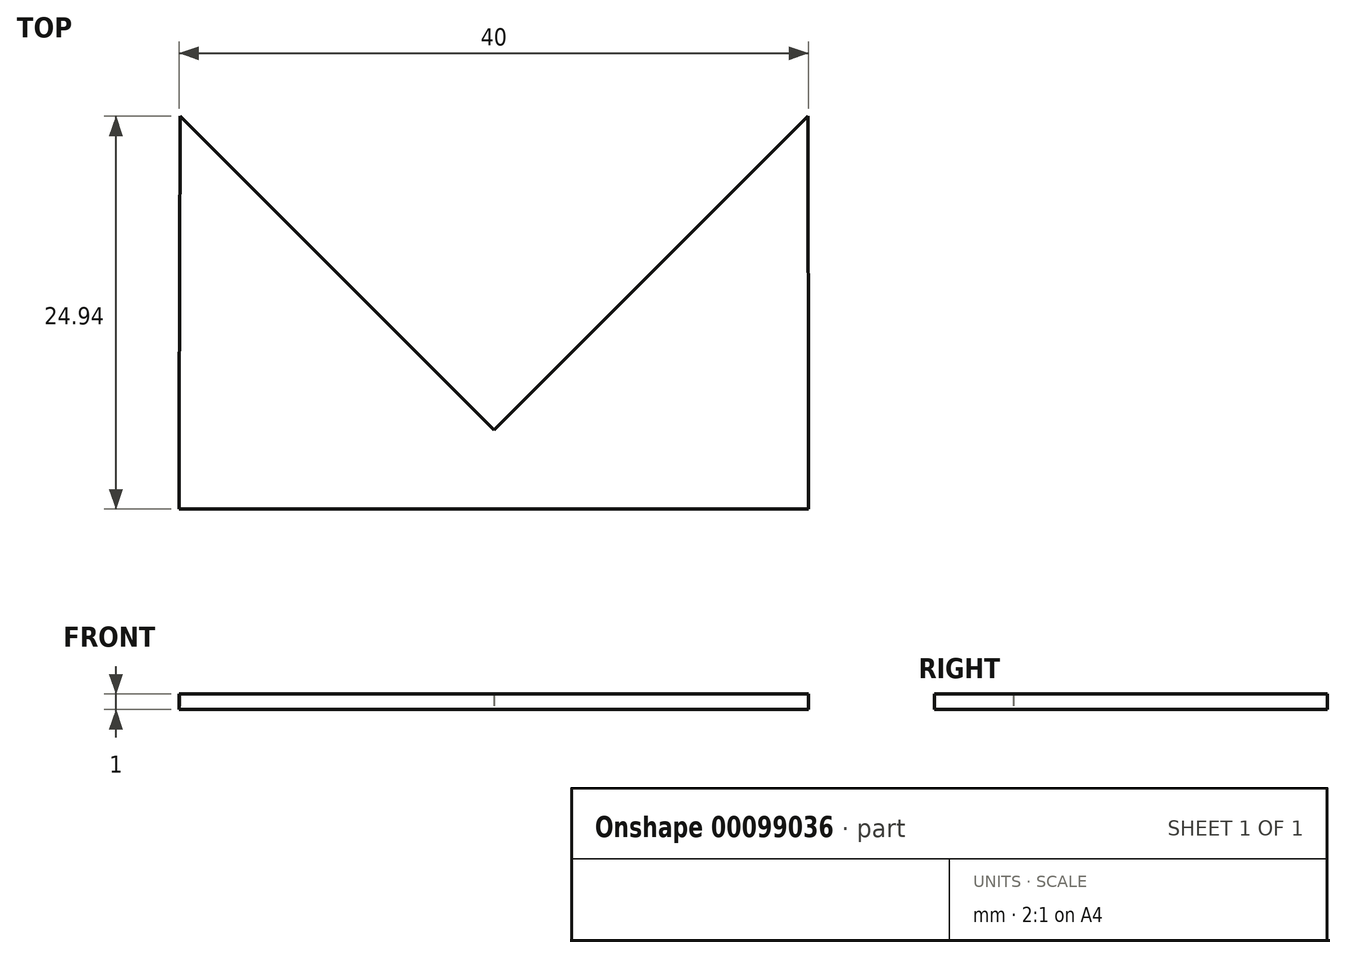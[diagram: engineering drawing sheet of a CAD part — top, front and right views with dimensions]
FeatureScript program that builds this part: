
annotation { "Feature Type Name" : "Feature", "Feature Type Description" : "" }
export const myFeature = defineFeature(function(context is Context, id is Id, definition is map)
    precondition{}
    {
        {
            var Q0;
            Q0=qCreatedBy(makeId("Top.planeOp"),FACE);
            var sketch = newSketch(context, id + "F0", { "sketchPlane" : qUnion([Q0])});
            skLineSegment(sketch, "E0.bottom", {"start": v(0, 0) * mm, "end": v(-20, 0) * mm});
            skLineSegment(sketch, "E0.top", {"start": v(0, 5) * mm, "end": v(-20, 5) * mm});
            skLineSegment(sketch, "E0.left", {"start": v(0, 0) * mm, "end": v(0, 5) * mm});
            skLineSegment(sketch, "E0.right", {"start": v(-20, 0) * mm, "end": v(-20, 5) * mm});
            skLineSegment(sketch, "E1", {"start": v(0, 5) * mm, "end": v(-19.94, 24.94) * mm});
            skLineSegment(sketch, "E2", {"start": v(-20, 5) * mm, "end": v(-19.94, 24.94) * mm});
            skLineSegment(sketch, "E3.MirrorCS", {"start": v(20, 0) * mm, "end": v(20, 5) * mm});
            skLineSegment(sketch, "E4.MirrorCS", {"start": v(20, 5) * mm, "end": v(19.94, 24.94) * mm});
            skLineSegment(sketch, "E5.MirrorCS", {"start": v(0, 5) * mm, "end": v(19.94, 24.94) * mm});
            skLineSegment(sketch, "E6.MirrorCS", {"start": v(0, 0) * mm, "end": v(20, 0) * mm});
            skLineSegment(sketch, "E7.MirrorCS", {"start": v(0, 5) * mm, "end": v(20, 5) * mm});
            skSolve(sketch);
        }
        {
            var Q0;
            Q0 = qSketchRegion(id + "F0", true);
            extrude(context, id + "F1", {"entities" : qUnion([Q0]), "depth" : 1 * mm});
        }
    });
